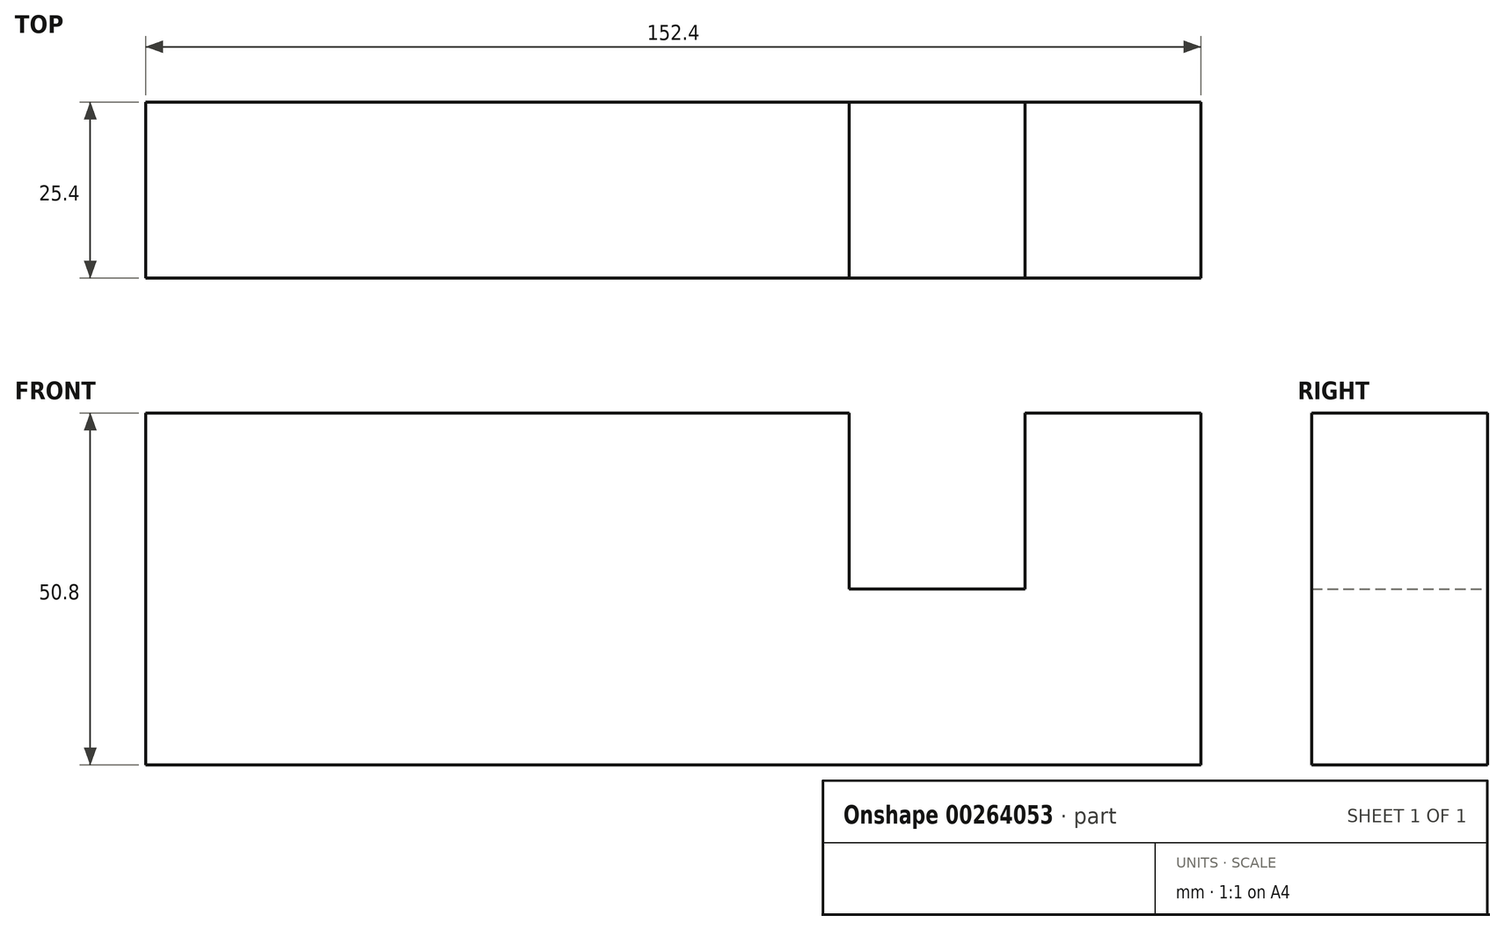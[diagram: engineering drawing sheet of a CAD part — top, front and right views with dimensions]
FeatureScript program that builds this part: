
annotation { "Feature Type Name" : "Feature", "Feature Type Description" : "" }
export const myFeature = defineFeature(function(context is Context, id is Id, definition is map)
    precondition{}
    {
        {
            var Q0;
            Q0=qCreatedBy(makeId("Front.planeOp"),FACE);
            var sketch = newSketch(context, id + "F0", { "sketchPlane" : qUnion([Q0])});
            skLineSegment(sketch, "E0", {"start": v(0, 0) * mm, "end": v(101.6, 0) * mm});
            skLineSegment(sketch, "E1", {"start": v(101.6, 0) * mm, "end": v(101.6, -25.4) * mm});
            skLineSegment(sketch, "E2", {"start": v(101.6, -25.4) * mm, "end": v(127, -25.4) * mm});
            skLineSegment(sketch, "E3", {"start": v(127, -25.4) * mm, "end": v(127, 0) * mm});
            skLineSegment(sketch, "E4", {"start": v(127, 0) * mm, "end": v(152.4, 0) * mm});
            skLineSegment(sketch, "E5", {"start": v(152.4, 0) * mm, "end": v(152.4, -50.8) * mm});
            skLineSegment(sketch, "E6", {"start": v(152.4, -50.8) * mm, "end": v(0, -50.8) * mm});
            skLineSegment(sketch, "E7", {"start": v(0, -50.8) * mm, "end": v(0, 0) * mm});
            skSolve(sketch);
        }
        {
            var Q0;
            Q0=makeQuery(id+"F0.imprint","IMPRINT",FACE,{"disambiguationData":[TD([[makeQuery(id+"F0.imprint","IMPRINT",EDGE,{"derivedFrom":sQuery(id+"F0.wireOp",EDGE,"E0")}),-1.0]])]});
            extrude(context, id + "F1", {"entities" : qUnion([Q0]), "depth" : 25.4 * mm});
        }
    });
